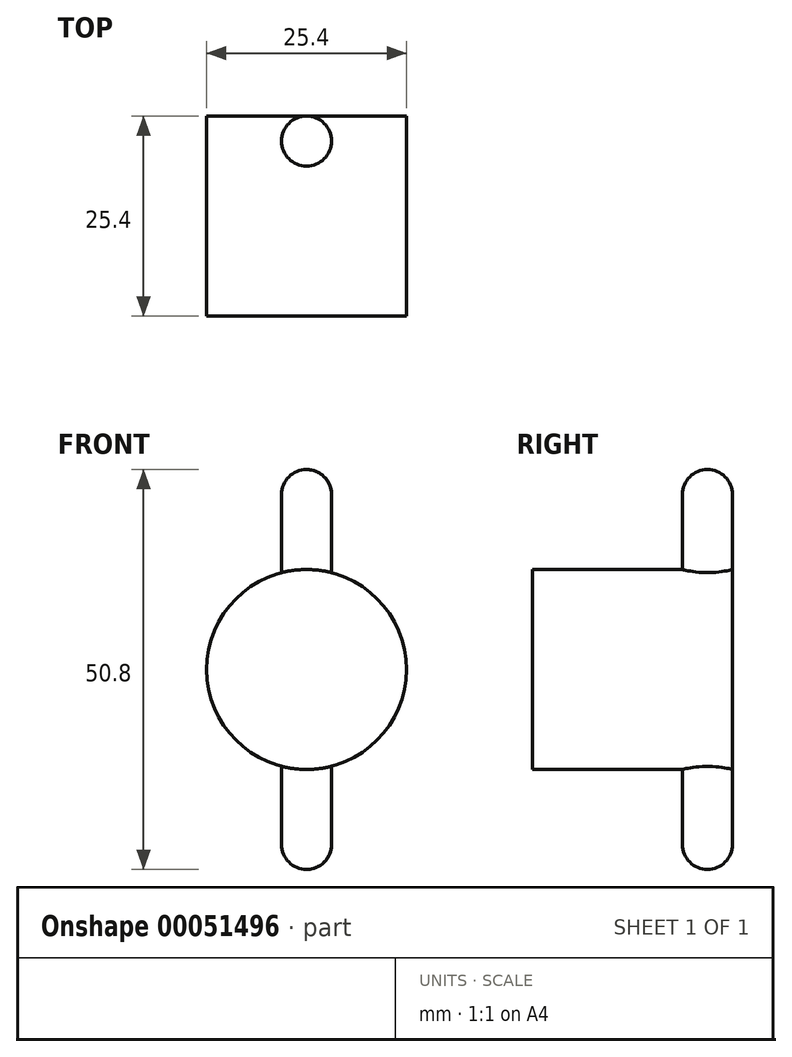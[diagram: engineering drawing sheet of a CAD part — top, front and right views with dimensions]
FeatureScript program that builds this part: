
annotation { "Feature Type Name" : "Feature", "Feature Type Description" : "" }
export const myFeature = defineFeature(function(context is Context, id is Id, definition is map)
    precondition{}
    {
        {
            var Q0;
            Q0=qCreatedBy(makeId("Front.planeOp"),FACE);
            var sketch = newSketch(context, id + "F0", { "sketchPlane" : qUnion([Q0])});
            skCircle(sketch, "E0", {"center": v(0, 0) * mm, "radius": 12.7 * mm});
            skSolve(sketch);
        }
        {
            var Q0;
            Q0 = qSketchRegion(id + "F0", true);
            extrude(context, id + "F1", {"entities" : qUnion([Q0]), "depth" : 25.4 * mm});
        }
        {
            var Q0;
            Q0=qCreatedBy(makeId("Top.planeOp"),FACE);
            var sketch = newSketch(context, id + "F2", { "sketchPlane" : qUnion([Q0])});
            skCircle(sketch, "E1", {"center": v(0, -3.18) * mm, "radius": 3.18 * mm});
            skSolve(sketch);
        }
        {
            var Q0;
            Q0 = qSketchRegion(id + "F2", true);
            extrude(context, id + "F3", {"entities" : qUnion([Q0]), "operationType" : NewBodyOperationType.ADD, "endBound" : BoundingType.SYMMETRIC, "depth" : 50.8 * mm});
        }
        {
            var Q0;
            Q0=makeQuery(id+"F3.opExtrude","CAP_EDGE",EDGE,{"disambiguationData":[OSD([sQuery(id+"F2.wireOp",EDGE,"E1")])],"isStart":true});
            var Q1;
            Q1=makeQuery(id+"F3.opExtrude","CAP_EDGE",EDGE,{"disambiguationData":[OSD([sQuery(id+"F2.wireOp",EDGE,"E1")])],"isStart":false});
            fillet(context, id + "F4", {"entities" : qUnion([Q0, Q1]), "radius" : 3.17 * mm, "tangentPropagation" : true, "allowEdgeOverflow" : false});
        }
    });
